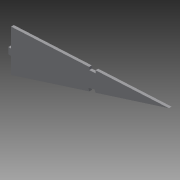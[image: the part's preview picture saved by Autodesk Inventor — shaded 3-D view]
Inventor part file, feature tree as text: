
AUTODESK INVENTOR PART (.ipt)
format: ipt  version: 2015 (Build 190159000, 159)  size: 121,856 bytes
history: native  units: in
note: dims shown in document units (in); Inventor stores cm internally (conversion verified against a paired STEP export)
features: sketch x4, extrude x3
ambient origin geometry x8: Origin, YZ Plane, XZ Plane, XY Plane, X Axis, Y Axis, Z Axis, Center Point
bodies: Solid1 (feature_tree)
feature tree (7):
  extrude  "Extrusion1"  Depth=0.125in TaperAngle=0.0deg
  extrude  "Extrusion3"  Depth=0.125in
  extrude  "Extrusion5"  Depth=0.3in
  sketch  "Sketch6"  dims[d34=0.125in d35=0.125in d36=0.3in d38=1.0in d39=0.0in d40=0.639in d41=0.4974in d43=1.042in d44=0.15in d45=3.802in d46=3.802in d47=0.15in d48=0.15in]
  sketch  "Sketch1"  dims[d0=1.959in d2=0.125in d3=0.0in]
  sketch  "Sketch3"  dims[d9=0.3in d11=0.125in]
  sketch  "Sketch5"  dims[d12=0.125in d13=0.0in d32=0.3in]
